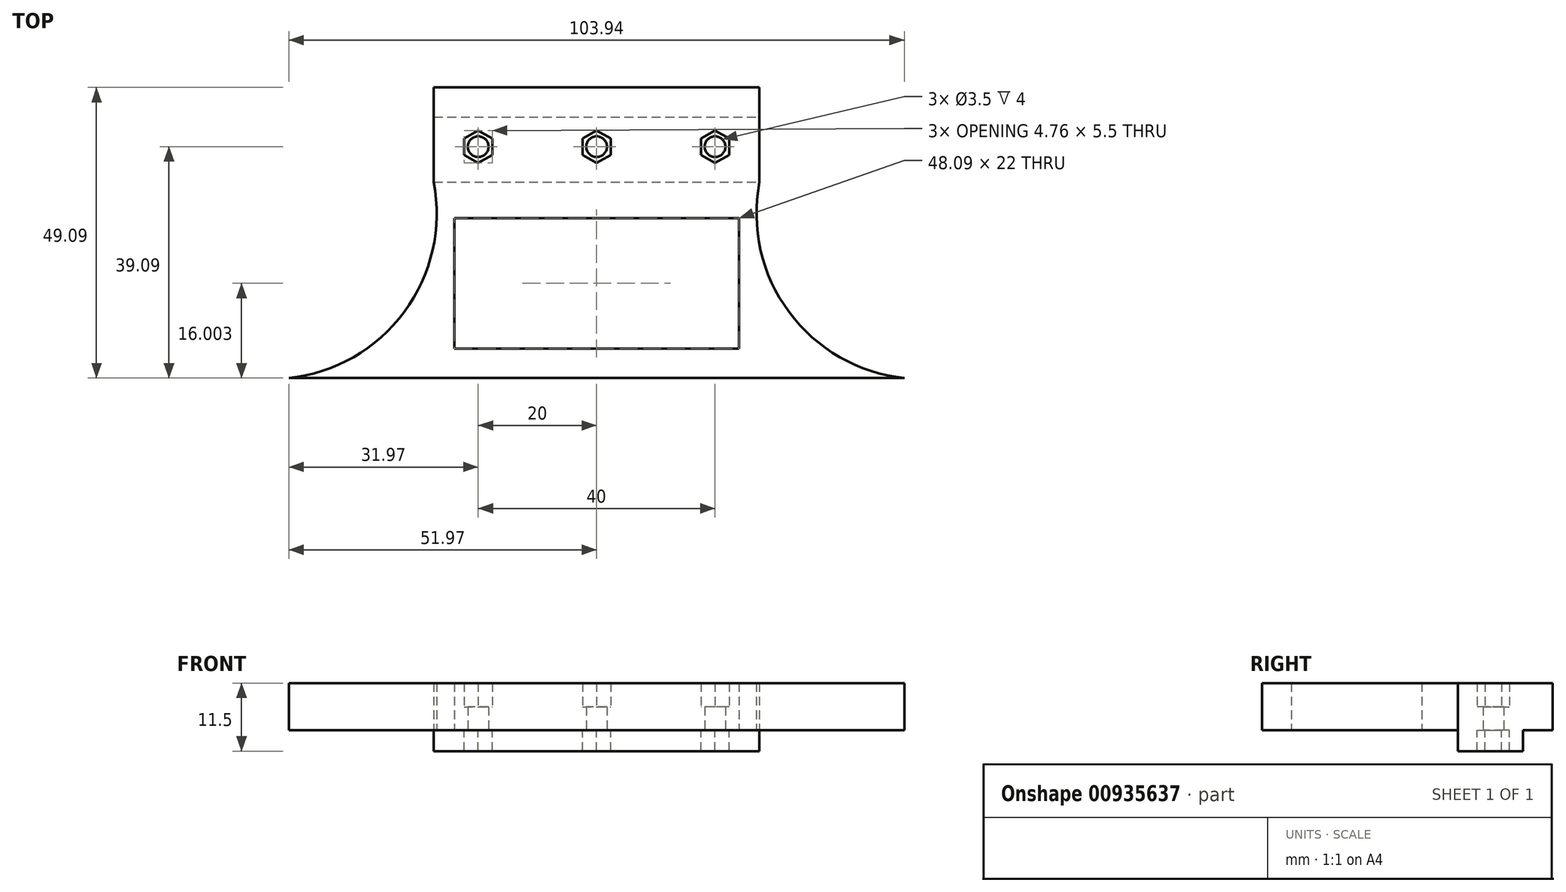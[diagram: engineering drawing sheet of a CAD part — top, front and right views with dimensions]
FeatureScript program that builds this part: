
annotation { "Feature Type Name" : "Feature", "Feature Type Description" : "" }
export const myFeature = defineFeature(function(context is Context, id is Id, definition is map)
    precondition{}
    {
        {
            var Q0;
            Q0=qCreatedBy(makeId("Top.planeOp"),FACE);
            var sketch = newSketch(context, id + "F0", { "sketchPlane" : qUnion([Q0])});
            skLineSegment(sketch, "E0.bottom", {"start": v(-27.5, 8) * mm, "end": v(27.5, 8) * mm});
            skLineSegment(sketch, "E0.top", {"start": v(-27.5, -8) * mm, "end": v(27.5, -8) * mm});
            skLineSegment(sketch, "E0.left", {"start": v(-27.5, 8) * mm, "end": v(-27.5, -8) * mm});
            skLineSegment(sketch, "E0.right", {"start": v(27.5, 8) * mm, "end": v(27.5, -8) * mm});
            skPoint(sketch, "E0.middle", {"position": v(0, 0) * mm});
            skLineSegment(sketch, "E1", {"start": v(-27.5, 3) * mm, "end": v(27.5, 3) * mm});
            skCircle(sketch, "E2.cCircle", {"center": v(0, -2) * mm, "radius": 2.38 * mm, "construction": true});
            skLineSegment(sketch, "E2.0", {"start": v(0, 0.75) * mm, "end": v(2.38, -0.62) * mm});
            skLineSegment(sketch, "E2.1", {"start": v(2.38, -0.62) * mm, "end": v(2.38, -3.37) * mm});
            skLineSegment(sketch, "E2.2", {"start": v(2.38, -3.37) * mm, "end": v(0, -4.75) * mm});
            skLineSegment(sketch, "E2.3", {"start": v(0, -4.75) * mm, "end": v(-2.38, -3.37) * mm});
            skLineSegment(sketch, "E2.4", {"start": v(-2.38, -3.37) * mm, "end": v(-2.38, -0.62) * mm});
            skLineSegment(sketch, "E2.5", {"start": v(-2.38, -0.63) * mm, "end": v(0, 0.75) * mm});
            skPoint(sketch, "E2.0.midPoint", {"position": v(1.2, 0.06) * mm});
            skCircle(sketch, "E3", {"center": v(0, -2) * mm, "radius": 1.75 * mm});
            skCircle(sketch, "E4", {"center": v(-20, -2) * mm, "radius": 1.75 * mm});
            skCircle(sketch, "E5.cCircle", {"center": v(-20, -2) * mm, "radius": 2.38 * mm, "construction": true});
            skLineSegment(sketch, "E5.0", {"start": v(-20, 0.75) * mm, "end": v(-17.62, -0.62) * mm});
            skLineSegment(sketch, "E5.1", {"start": v(-17.62, -0.62) * mm, "end": v(-17.62, -3.38) * mm});
            skLineSegment(sketch, "E5.2", {"start": v(-17.62, -3.38) * mm, "end": v(-20, -4.75) * mm});
            skLineSegment(sketch, "E5.3", {"start": v(-20, -4.75) * mm, "end": v(-22.38, -3.38) * mm});
            skLineSegment(sketch, "E5.4", {"start": v(-22.38, -3.38) * mm, "end": v(-22.38, -0.62) * mm});
            skLineSegment(sketch, "E5.5", {"start": v(-22.38, -0.62) * mm, "end": v(-20, 0.75) * mm});
            skPoint(sketch, "E5.0.midPoint", {"position": v(-18.8, 0.06) * mm});
            skLineSegment(sketch, "E6.MirrorCS", {"start": v(20, 0.75) * mm, "end": v(17.62, -0.62) * mm});
            skLineSegment(sketch, "E7.MirrorCS", {"start": v(22.38, -0.62) * mm, "end": v(20, 0.75) * mm});
            skLineSegment(sketch, "E8.MirrorCS", {"start": v(22.38, -3.38) * mm, "end": v(22.38, -0.62) * mm});
            skLineSegment(sketch, "E9.MirrorCS", {"start": v(20, -4.75) * mm, "end": v(22.38, -3.38) * mm});
            skLineSegment(sketch, "E10.MirrorCS", {"start": v(17.62, -3.38) * mm, "end": v(20, -4.75) * mm});
            skCircle(sketch, "E11.MirrorC", {"center": v(20, -2) * mm, "radius": 2.38 * mm, "construction": true});
            skLineSegment(sketch, "E12.MirrorCS", {"start": v(17.62, -0.62) * mm, "end": v(17.62, -3.38) * mm});
            skCircle(sketch, "E13.MirrorC", {"center": v(20, -2) * mm, "radius": 1.75 * mm});
            skArc(sketch, "E14", {"start": v(-58, -41.09) * mm, "mid": v(-34.4, -32.23) * mm, "end": v(-27.5, -8) * mm});
            skArc(sketch, "E15.MirrorCS", {"start": v(58, -41.09) * mm, "mid": v(34.4, -32.23) * mm, "end": v(27.5, -8) * mm});
            skLineSegment(sketch, "E16", {"start": v(-58, -41.09) * mm, "end": v(58, -41.09) * mm});
            skLineSegment(sketch, "E17.bottom", {"start": v(-24.04, -14.09) * mm, "end": v(24.04, -14.09) * mm});
            skLineSegment(sketch, "E17.top", {"start": v(-24.04, -36.09) * mm, "end": v(24.04, -36.09) * mm});
            skLineSegment(sketch, "E17.left", {"start": v(-24.04, -14.09) * mm, "end": v(-24.04, -36.09) * mm});
            skLineSegment(sketch, "E17.right", {"start": v(24.04, -14.09) * mm, "end": v(24.04, -36.09) * mm});
            skSolve(sketch);
        }
        {
            var Q0;
            {var subQ0=sQuery(id+"F0.wireOp",EDGE,"E0.top");Q0=makeQuery(id+"F0.imprint","IMPRINT",FACE,{"disambiguationData":[TD([[makeQuery(id+"F0.imprint","IMPRINT",EDGE,{"derivedFrom":subQ0}),1.0]])]});}
            var Q1;
            {var subQ0=sQuery(id+"F0.wireOp",EDGE,"E0.bottom");Q1=makeQuery(id+"F0.imprint","IMPRINT",FACE,{"disambiguationData":[TD([[makeQuery(id+"F0.imprint","IMPRINT",EDGE,{"derivedFrom":subQ0}),-1.0]])]});}
            extrude(context, id + "F1", {"entities" : qUnion([Q0, Q1]), "depth" : 8 * mm, "offsetDistance" : 25 * mm});
        }
        {
            var Q0;
            Q0=makeQuery(id+"F0.imprint","IMPRINT",FACE,{"disambiguationData":[TD([[makeQuery(id+"F0.imprint","IMPRINT",EDGE,{"derivedFrom":sQuery(id+"F0.wireOp",EDGE,"E2.0")}),-1.0]])]});
            var Q1;
            Q1=makeQuery(id+"F0.imprint","IMPRINT",FACE,{"disambiguationData":[TD([[makeQuery(id+"F0.imprint","IMPRINT",EDGE,{"derivedFrom":sQuery(id+"F0.wireOp",EDGE,"E6.MirrorCS")}),1.0]])]});
            var Q2;
            Q2=makeQuery(id+"F0.imprint","IMPRINT",FACE,{"disambiguationData":[TD([[makeQuery(id+"F0.imprint","IMPRINT",EDGE,{"derivedFrom":sQuery(id+"F0.wireOp",EDGE,"E4")}),-1.0]])]});
            extrude(context, id + "F2", {"entities" : qUnion([Q0, Q1, Q2]), "operationType" : NewBodyOperationType.ADD, "depth" : 4 * mm, "offsetDistance" : 25 * mm});
        }
        {
            var Q0;
            {var subQ0=sQuery(id+"F0.wireOp",EDGE,"E0.top");Q0=makeQuery(id+"F0.imprint","IMPRINT",FACE,{"disambiguationData":[TD([[makeQuery(id+"F0.imprint","IMPRINT",EDGE,{"derivedFrom":subQ0}),1.0]])]});}
            extrude(context, id + "F3", {"entities" : qUnion([Q0]), "operationType" : NewBodyOperationType.ADD, "oppositeDirection" : true, "depth" : 3.5 * mm, "offsetDistance" : 25 * mm});
        }
        {
            var Q0;
            {var subQ0=sQuery(id+"F0.wireOp",EDGE,"E0.top");Q0=makeQuery(id+"F0.imprint","IMPRINT",FACE,{"disambiguationData":[TD([[makeQuery(id+"F0.imprint","IMPRINT",EDGE,{"derivedFrom":subQ0}),-1.0]])]});}
            extrude(context, id + "F4", {"entities" : qUnion([Q0]), "operationType" : NewBodyOperationType.ADD, "depth" : 8 * mm, "offsetDistance" : 25 * mm});
        }
    });
